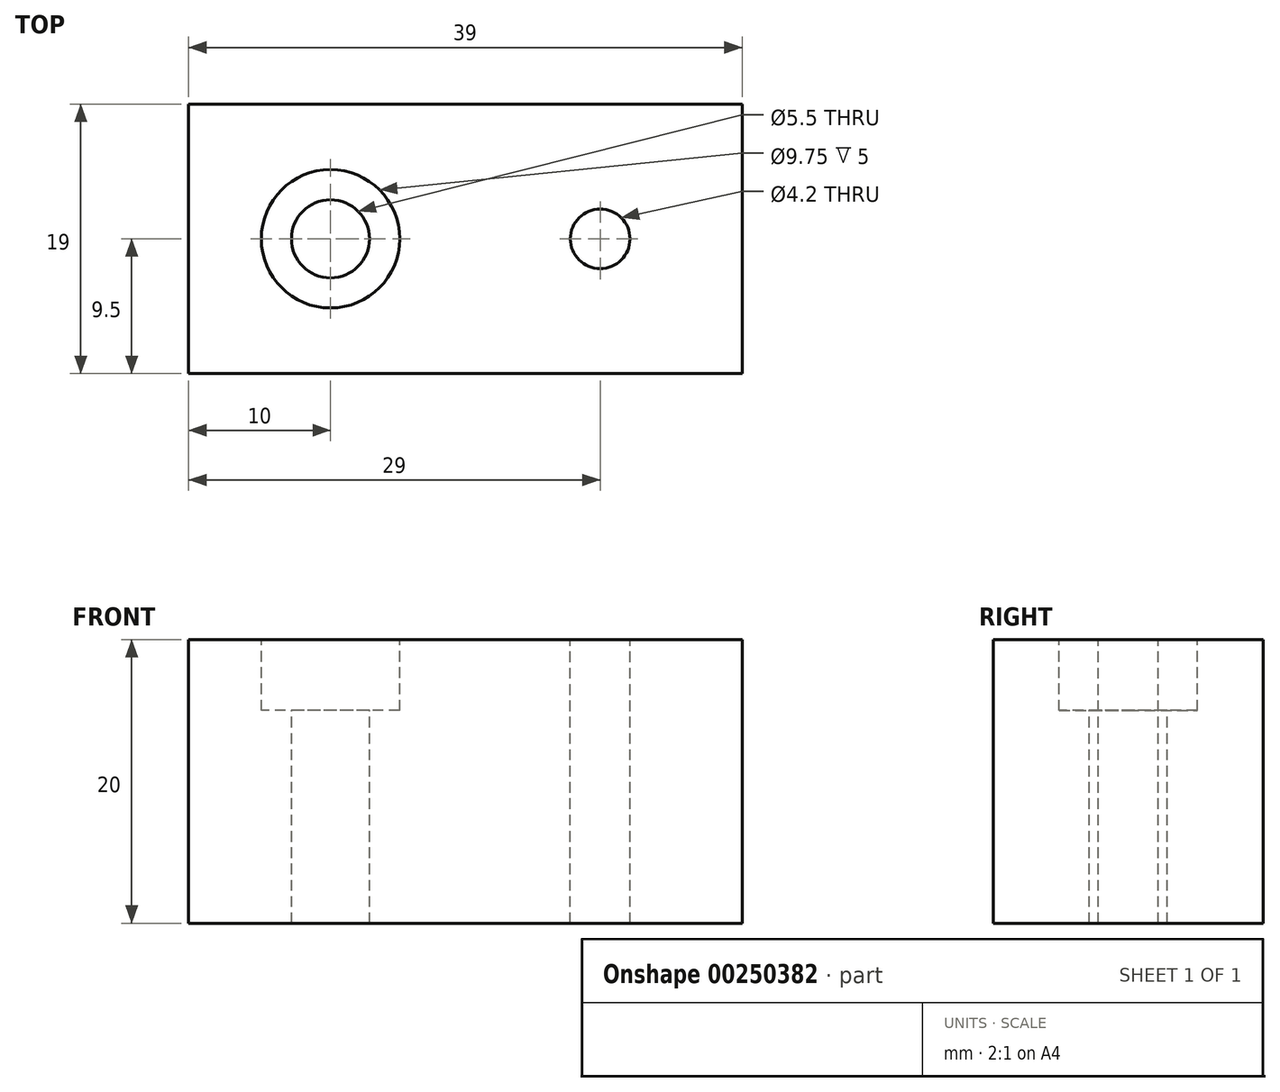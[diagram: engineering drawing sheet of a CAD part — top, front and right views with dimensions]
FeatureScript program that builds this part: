
annotation { "Feature Type Name" : "Feature", "Feature Type Description" : "" }
export const myFeature = defineFeature(function(context is Context, id is Id, definition is map)
    precondition{}
    {
        {
            var Q0;
            Q0=qCreatedBy(makeId("Top.planeOp"),FACE);
            var sketch = newSketch(context, id + "F0", { "sketchPlane" : qUnion([Q0])});
            skLineSegment(sketch, "E0.bottom", {"start": v(-19.5, 9.5) * mm, "end": v(19.5, 9.5) * mm});
            skLineSegment(sketch, "E0.top", {"start": v(-19.5, -9.5) * mm, "end": v(19.5, -9.5) * mm});
            skLineSegment(sketch, "E0.left", {"start": v(-19.5, 9.5) * mm, "end": v(-19.5, -9.5) * mm});
            skLineSegment(sketch, "E0.right", {"start": v(19.5, 9.5) * mm, "end": v(19.5, -9.5) * mm});
            skPoint(sketch, "E1", {"position": v(-9.5, 0) * mm});
            skPoint(sketch, "E2", {"position": v(9.5, 0) * mm});
            skSolve(sketch);
        }
        {
            var Q0;
            Q0=makeQuery(id+"F0.imprint","IMPRINT",FACE,{"disambiguationData":[TD([[makeQuery(id+"F0.imprint","IMPRINT",EDGE,{"derivedFrom":sQuery(id+"F0.wireOp",EDGE,"E0.bottom")}),-1.0]])]});
            extrude(context, id + "F1", {"entities" : qUnion([Q0]), "oppositeDirection" : true, "depth" : 20 * mm});
        }
        {
            var Q0;
            Q0=sQuery(id+"F0.wireOp",VERTEX,"E1");
            var Q1;
            Q1=makeQuery(id+"F1.opExtrude","SWEPT_BODY",BODY,{"disambiguationData":[OSD([sQuery(id+"F0.wireOp",EDGE,"E0.bottom"),sQuery(id+"F0.wireOp",EDGE,"E0.top"),sQuery(id+"F0.wireOp",EDGE,"E0.left"),sQuery(id+"F0.wireOp",EDGE,"E0.right")])]});
            hole(context, id + "F2", {"style" : HoleStyle.C_BORE, "endStyle" : HoleEndStyle.BLIND, "standardTappedOrClearance" : lookupTablePath({ "standard" : "ISO", "fit" : "Normal", "size" : "M5", "type" : "Clearance" }), "standardBlindInLast" : lookupTablePath({ "fit" : "Standard", "standard" : "ISO", "size" : "M5", "type" : "Clearance" }), "holeDiameter" : 5.5 * mm, "cBoreDiameter" : 9.75 * mm, "cBoreDepth" : 5 * mm, "holeDepth" : 20 * mm, "tappedDepth" : 12 * mm, "tapClearance" : 3, "locations" : qUnion([Q0]), "scope" : qUnion([Q1])});
        }
        {
            var Q0;
            Q0=sQuery(id+"F0.wireOp",VERTEX,"E2");
            var Q1;
            Q1=makeQuery(id+"F1.opExtrude","SWEPT_BODY",BODY,{"disambiguationData":[OSD([sQuery(id+"F0.wireOp",EDGE,"E0.bottom"),sQuery(id+"F0.wireOp",EDGE,"E0.top"),sQuery(id+"F0.wireOp",EDGE,"E0.left"),sQuery(id+"F0.wireOp",EDGE,"E0.right")])]});
            hole(context, id + "F3", {"style" : HoleStyle.SIMPLE, "endStyle" : HoleEndStyle.BLIND, "standardTappedOrClearance" : lookupTablePath({ "standard" : "ISO", "engagement" : "75%", "pitch" : "0.8 mm", "size" : "M5", "type" : "Tapped" }), "standardBlindInLast" : lookupTablePath({ "standard" : "ISO", "engagement" : "75%", "pitch" : "0.8 mm", "size" : "M5", "type" : "Tapped" }), "holeDiameter" : 4.2 * mm, "showTappedDepth" : true, "holeDepth" : 22.4 * mm, "tappedDepth" : 20 * mm, "tapClearance" : 3, "locations" : qUnion([Q0]), "scope" : qUnion([Q1]), "majorDiameter" : 5 * mm});
        }
    });
